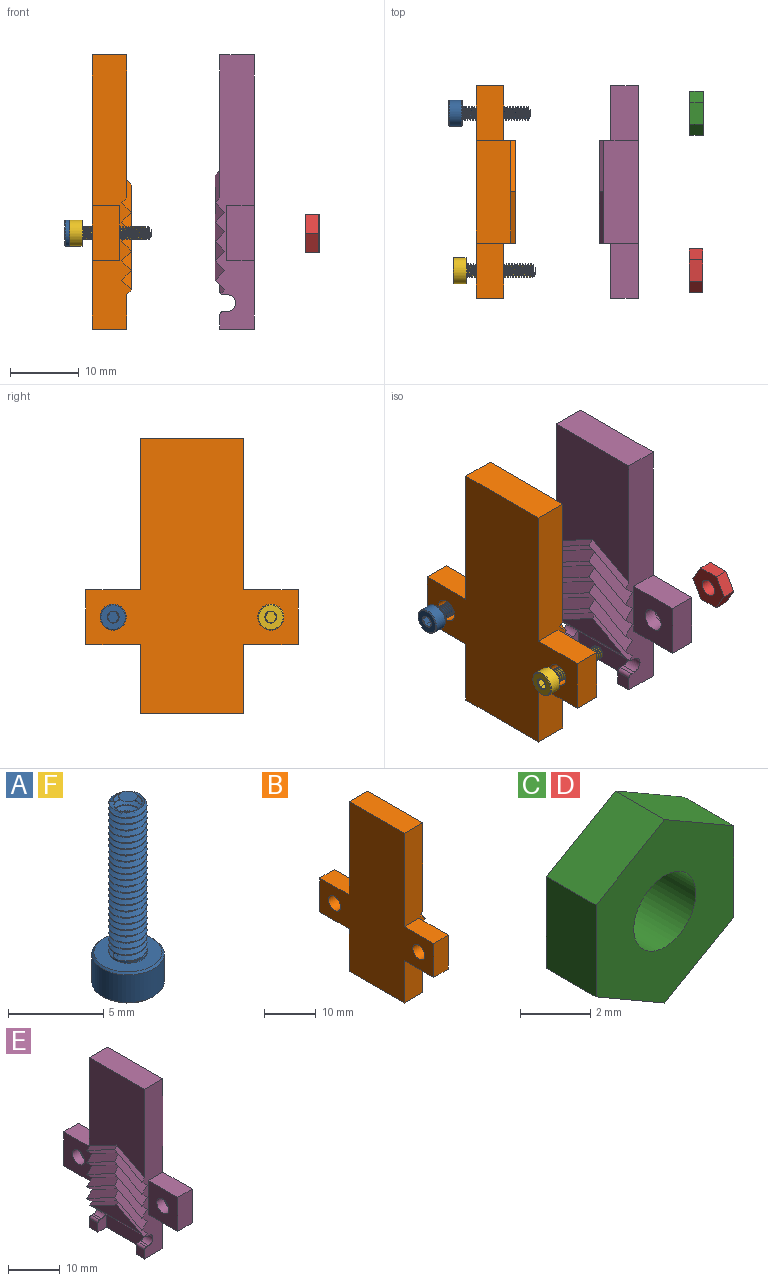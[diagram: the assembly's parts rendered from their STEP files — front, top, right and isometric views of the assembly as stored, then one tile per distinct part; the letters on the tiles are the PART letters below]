
ASSEMBLY  parts=6 mates=8
PART A: 49 faces, bbox 4.1x4.1x12.3 mm
  f0: cylinder r=1mm len=1.99mm, axis (0,0,1), area 0.1mm2, adj f1,f25,f26,f28
  f1: cylinder r=1mm len=2mm, axis (0,0,1), area 0.3mm2, adj f0,f2,f25,f26
  f2: cylinder r=1mm len=2mm, axis (0,0,1), area 0.3mm2, adj f1,f3,f25,f26
  f3: cylinder r=1mm len=2mm, axis (0,0,1), area 0.3mm2, adj f2,f4,f25,f26
  f4: cylinder r=1mm len=2mm, axis (0,0,1), area 0.3mm2, adj f3,f5,f25,f26
  f5: cylinder r=1mm len=2mm, axis (0,0,1), area 0.3mm2, adj f4,f6,f25,f26
  f6: cylinder r=1mm len=2mm, axis (0,0,1), area 0.3mm2, adj f5,f7,f25,f26
  f7: cylinder r=1mm len=2mm, axis (0,0,1), area 0.3mm2, adj f6,f8,f25,f26
  f8: cylinder r=1mm len=2mm, axis (0,0,1), area 0.3mm2, adj f7,f9,f25,f26
  f9: cylinder r=1mm len=2mm, axis (0,0,1), area 0.3mm2, adj f8,f10,f25,f26
  f10: cylinder r=1mm len=2mm, axis (0,0,1), area 0.3mm2, adj f9,f11,f25,f26
  f11: cylinder r=1mm len=2mm, axis (0,0,1), area 0.3mm2, adj f10,f12,f25,f26
  f12: cylinder r=1mm len=2mm, axis (0,0,1), area 0.3mm2, adj f11,f13,f25,f26
  f13: cylinder r=1mm len=2mm, axis (0,0,1), area 0.3mm2, adj f12,f14,f25,f26
  f14: cylinder r=1mm len=2mm, axis (0,0,1), area 0.3mm2, adj f13,f15,f25,f26
  f15: cylinder r=1mm len=2mm, axis (0,0,1), area 0.3mm2, adj f14,f16,f25,f26
  f16: cylinder r=1mm len=2mm, axis (0,0,1), area 0.3mm2, adj f15,f17,f25,f26
  f17: cylinder r=1mm len=2mm, axis (0,0,1), area 0.3mm2, adj f16,f18,f25,f26
  f18: cylinder r=1mm len=2mm, axis (0,0,1), area 0.3mm2, adj f17,f19,f25,f26
  f19: cylinder r=1mm len=2mm, axis (0,0,1), area 0.3mm2, adj f18,f20,f25,f26
  f20: cylinder r=1mm len=2mm, axis (0,0,1), area 0.3mm2, adj f19,f21,f25,f26
  f21: cylinder r=1mm len=2mm, axis (0,0,1), area 0.3mm2, adj f20,f22,f25,f26
  f22: cylinder r=1mm len=2mm, axis (0,0,1), area 0.3mm2, adj f21,f23,f25,f26
  f23: cylinder r=1mm len=2mm, axis (0,0,1), area 0.3mm2, adj f22,f24,f25,f26
  f24: cylinder r=1mm len=2mm, axis (0,0,1), area 0.8mm2, adj f23,f25,f26,f32,f48
  f25: bspline ~10.08x2.31mm, area 39.4mm2, adj f0,f1,f2,f3,f4,f5,f6,f7
  f26: bspline ~9.88x2.31mm, area 39.3mm2, adj f0,f1,f2,f3,f4,f5,f6,f7
  f27: cylinder r=0.74mm len=9.61mm, axis (0,0,-1), area -0.5mm2, adj f25,f26,f28,f48
  f28: cone r=0.49mm half-angle=55deg, axis (0,0,-1), area 2mm2, adj f0,f25,f26,f27,f29
  f29: plane 0.97x0.97mm, normal (0,0,1), area 0.7mm2, adj f28
  f30: cylinder r=1.9mm len=3.8mm, axis (0,0,1), area 21.2mm2, adj f46,f47
  f31: plane 3.57x3.57mm, normal (0,0,-1), area 7.7mm2, adj f33,f34,f35,f36,f37,f38,f46
  f32: plane 3.57x3.57mm, normal (0,0,1), area 6.9mm2, adj f24,f47
  f33: cone r=0.87mm half-angle=45deg, axis (0,0,-1), area 0mm2, adj f31,f40
  f34: cone r=0.87mm half-angle=45deg, axis (0,0,-1), area 0mm2, adj f31,f41
  f35: cone r=0.87mm half-angle=45deg, axis (0,0,-1), area 0mm2, adj f31,f42
  f36: cone r=0.87mm half-angle=45deg, axis (0,0,-1), area 0mm2, adj f31,f43
  f37: cone r=0.87mm half-angle=45deg, axis (0,0,-1), area 0mm2, adj f31,f44
  f38: cone r=0.87mm half-angle=45deg, axis (0,0,-1), area 0mm2, adj f31,f45
  f39: plane 1.73x1.5mm, normal (0,0,-1), area 1.9mm2, adj f40,f41,f42,f43,f44,f45
  f40: plane 1.45x1.08mm, normal (-0.5,-0.87,0), area 0.9mm2, adj f33,f39,f41,f45
  f41: plane 1.45x1.2mm, normal (-1,0,0), area 0.9mm2, adj f34,f39,f40,f42
  f42: plane 1.45x1.08mm, normal (-0.5,0.87,0), area 0.9mm2, adj f35,f39,f41,f43
  f43: plane 1.45x1.08mm, normal (0.5,0.87,0), area 0.9mm2, adj f36,f39,f42,f44
  f44: plane 1.45x1.2mm, normal (1,0,0), area 0.9mm2, adj f37,f39,f43,f45
  f45: plane 1.45x1.08mm, normal (0.5,-0.87,0), area 0.9mm2, adj f38,f39,f40,f44
  f46: cone r=1.79mm half-angle=45deg, axis (0,0,1), area 1.9mm2, adj f30,f31
  f47: cone r=1.9mm half-angle=45deg, axis (0,0,-1), area 1.9mm2, adj f30,f32
  f48: cone r=1mm half-angle=67.5deg, axis (0,0,-1), area 0.8mm2, adj f24,f25,f26,f27
PART B: 39 faces, bbox 5.7x31x40 mm
  f0: plane 40x5.71mm, normal (0,-1,0), area 168mm2, adj f1,f2,f3,f4,f5,f6,f7,f8
  f1: plane 40x31mm, normal (-1,0,0), area 710.9mm2, adj f0,f2,f16,f17,f19,f20,f21,f22
  f2: plane 15x5mm, normal (0,0,1), area 75mm2, adj f0,f1,f3,f22
  f3: plane 20.86x15mm, normal (1,0,0), area 282.9mm2, adj f0,f2,f4,f22,f23
  f4: plane 7.5x4.71mm, normal (0.66,0.35,-0.66), area 8mm2, adj f0,f3,f5,f23
  f5: plane 7.5x5.41mm, normal (0.66,-0.35,0.66), area 16mm2, adj f0,f4,f6,f24
  f6: plane 7.5x5.41mm, normal (0.66,0.35,-0.66), area 16mm2, adj f0,f5,f7,f25
  f7: plane 7.5x5.41mm, normal (0.66,-0.35,0.66), area 16mm2, adj f0,f6,f8,f26
  f8: plane 7.5x5.41mm, normal (0.66,0.35,-0.66), area 16mm2, adj f0,f7,f9,f27
  f9: plane 7.5x5.41mm, normal (0.66,-0.35,0.66), area 16mm2, adj f0,f8,f10,f28
  f10: plane 7.5x5.41mm, normal (0.66,0.35,-0.66), area 16mm2, adj f0,f9,f11,f29
  f11: plane 7.5x5.41mm, normal (0.66,-0.35,0.66), area 16mm2, adj f0,f10,f12,f30
  f12: plane 7.5x5.41mm, normal (0.66,0.35,-0.66), area 16mm2, adj f0,f11,f13,f31
  f13: plane 7.5x5.41mm, normal (0.66,-0.35,0.66), area 16mm2, adj f0,f12,f14,f32
  f14: plane 7.5x4.71mm, normal (0.66,0.35,-0.66), area 8mm2, adj f0,f13,f15,f33
  f15: plane 15x9mm, normal (1,0,0), area 105mm2, adj f0,f14,f16,f22,f33
  f16: plane 15x5mm, normal (0,0,-1), area 75mm2, adj f0,f1,f15,f22
  f17: plane 8x4mm, normal (0,0,-1), area 32mm2, adj f0,f1,f18,f20
  f18: plane 8x8mm, normal (1,0,0), area 55.4mm2, adj f0,f17,f19,f20,f21
  f19: plane 8x4mm, normal (0,0,1), area 32mm2, adj f0,f1,f18,f20
  f20: plane 8x4mm, normal (0,-1,0), area 32mm2, adj f1,f17,f18,f19
  f21: cylinder r=1.65mm len=4mm, axis (-1,0,0), area 41.5mm2, adj f1,f18
  f22: plane 40x5.71mm, normal (0,1,0), area 168mm2, adj f1,f2,f3,f15,f16,f23,f24,f25
  f23: plane 7.5x4.71mm, normal (0.66,-0.35,-0.66), area 8mm2, adj f3,f4,f22,f24
  f24: plane 7.5x5.41mm, normal (0.66,0.35,0.66), area 16mm2, adj f5,f22,f23,f25
  f25: plane 7.5x5.41mm, normal (0.66,-0.35,-0.66), area 16mm2, adj f6,f22,f24,f26
  f26: plane 7.5x5.41mm, normal (0.66,0.35,0.66), area 16mm2, adj f7,f22,f25,f27
  f27: plane 7.5x5.41mm, normal (0.66,-0.35,-0.66), area 16mm2, adj f8,f22,f26,f28
  f28: plane 7.5x5.41mm, normal (0.66,0.35,0.66), area 16mm2, adj f9,f22,f27,f29
  f29: plane 7.5x5.41mm, normal (0.66,-0.35,-0.66), area 16mm2, adj f10,f22,f28,f30
  f30: plane 7.5x5.41mm, normal (0.66,0.35,0.66), area 16mm2, adj f11,f22,f29,f31
  f31: plane 7.5x5.41mm, normal (0.66,-0.35,-0.66), area 16mm2, adj f12,f22,f30,f32
  f32: plane 7.5x5.41mm, normal (0.66,0.35,0.66), area 16mm2, adj f13,f22,f31,f33
  f33: plane 7.5x4.71mm, normal (0.66,-0.35,-0.66), area 8mm2, adj f14,f15,f22,f32
  f34: plane 8x4mm, normal (0,0,-1), area 32mm2, adj f1,f22,f35,f37
  f35: plane 8x8mm, normal (1,0,0), area 55.4mm2, adj f22,f34,f36,f37,f38
  f36: plane 8x4mm, normal (0,0,1), area 32mm2, adj f1,f22,f35,f37
  f37: plane 8x4mm, normal (0,1,0), area 32mm2, adj f1,f34,f35,f36
  f38: cylinder r=1.65mm len=4mm, axis (-1,0,0), area 41.5mm2, adj f1,f35
PART C: 9 faces, bbox 5.6x2x6.4 mm
  f0: plane 2.78x2mm, normal (0.5,0,-0.87), area 6.4mm2, adj f1,f6,f7,f8
  f1: plane 3.2x2mm, normal (1,0,0), area 6.4mm2, adj f0,f2,f7,f8
  f2: plane 2.78x2mm, normal (0.5,0,0.87), area 6.4mm2, adj f1,f3,f7,f8
  f3: plane 2.78x2mm, normal (-0.5,0,0.87), area 6.4mm2, adj f2,f4,f7,f8
  f4: plane 3.2x2mm, normal (-1,0,0), area 6.4mm2, adj f3,f6,f7,f8
  f5: cylinder r=1.25mm len=2.5mm, axis (0,1,0), area 15.7mm2, adj f7,f8
  f6: plane 2.78x2mm, normal (-0.5,0,-0.87), area 6.4mm2, adj f0,f4,f7,f8
  f7: plane 6.41x5.55mm, normal (0,-1,0), area 21.8mm2, adj f0,f1,f2,f3,f4,f5,f6
  f8: plane 6.41x5.55mm, normal (0,1,0), area 21.8mm2, adj f0,f1,f2,f3,f4,f5,f6
PART D: same geometry as C
PART E: 65 faces, bbox 5.7x31x40 mm
  f0: plane 2.3x2.1mm, normal (-1,0,0), area 4.8mm2, adj f1,f4,f6,f62
  f1: plane 15x5mm, normal (0,0,-1), area 51.1mm2, adj f0,f6,f7,f8,f9,f62,f63,f64
  f2: plane 2.3x0.6mm, normal (0,0,1), area 1.4mm2, adj f3,f4,f6,f62
  f3: cylinder r=1.2mm len=15mm, axis (0,-1,0), area 36.9mm2, adj f2,f6,f7,f58,f59,f62,f63,f64
  f4: cylinder r=0.5mm len=2.3mm, axis (0,-1,0), area 1.8mm2, adj f0,f2,f6,f62
  f5: plane 13.13x3.5mm, normal (-1,0,0), area 23mm2, adj f10,f35,f61
  f6: plane 40x5.71mm, normal (0,-1,0), area 163mm2, adj f0,f1,f2,f3,f4,f8,f10,f11
  f7: plane 40x5.71mm, normal (0,1,0), area 163mm2, adj f1,f3,f8,f9,f21,f22,f35,f36
  f8: plane 40x31mm, normal (1,0,0), area 674.6mm2, adj f1,f6,f7,f22,f23,f24,f26,f27
  f9: plane 2.3x2.1mm, normal (-1,0,0), area 4.8mm2, adj f1,f7,f60,f63
  f10: plane 7.5x4.56mm, normal (-0.66,-0.35,0.66), area 7.9mm2, adj f5,f6,f11,f35,f61
  f11: plane 7.5x5.41mm, normal (-0.66,0.35,-0.66), area 16mm2, adj f6,f10,f12,f36
  f12: plane 7.5x5.41mm, normal (-0.66,-0.35,0.66), area 16mm2, adj f6,f11,f13,f37
  f13: plane 7.5x5.41mm, normal (-0.66,0.35,-0.66), area 16mm2, adj f6,f12,f14,f38
  f14: plane 7.5x5.41mm, normal (-0.66,-0.35,0.66), area 16mm2, adj f6,f13,f15,f39
  f15: plane 7.5x5.41mm, normal (-0.66,0.35,-0.66), area 16mm2, adj f6,f14,f16,f40
  f16: plane 7.5x5.41mm, normal (-0.66,-0.35,0.66), area 16mm2, adj f6,f15,f17,f41
  f17: plane 7.5x5.41mm, normal (-0.66,0.35,-0.66), area 16mm2, adj f6,f16,f18,f42
  f18: plane 7.5x5.41mm, normal (-0.66,-0.35,0.66), area 16mm2, adj f6,f17,f19,f43
  f19: plane 7.5x5.41mm, normal (-0.66,0.35,-0.66), area 16mm2, adj f6,f18,f20,f44
  f20: plane 7.5x4.71mm, normal (-0.66,-0.35,0.66), area 8mm2, adj f6,f19,f21,f45
  f21: plane 20.86x15mm, normal (-1,0,0), area 282.9mm2, adj f6,f7,f20,f22,f45
  f22: plane 15x5mm, normal (0,0,1), area 75mm2, adj f6,f7,f8,f21
  f23: plane 8x4mm, normal (0,0,-1), area 32mm2, adj f6,f8,f25,f26
  f24: plane 8x4mm, normal (0,0,1), area 32mm2, adj f6,f8,f25,f26
  f25: plane 8x8mm, normal (-1,0,0), area 55.4mm2, adj f6,f23,f24,f26,f34
  f26: plane 8x4mm, normal (0,-1,0), area 32mm2, adj f8,f23,f24,f25
  f27: plane 2.78x2mm, normal (0,-0.87,-0.5), area 6.4mm2, adj f8,f28,f32,f33
  f28: plane 3.2x2mm, normal (0,0,-1), area 6.4mm2, adj f8,f27,f29,f33
  f29: plane 2.77x2mm, normal (0,0.87,-0.5), area 6.4mm2, adj f8,f28,f30,f33
  f30: plane 2.78x2mm, normal (0,0.87,0.5), area 6.4mm2, adj f8,f29,f31,f33
  f31: plane 3.2x2mm, normal (0,0,1), area 6.4mm2, adj f8,f30,f32,f33
  f32: plane 2.77x2mm, normal (0,-0.87,0.5), area 6.4mm2, adj f8,f27,f31,f33
  f33: plane 6.41x5.56mm, normal (1,0,0), area 18.1mm2, adj f27,f28,f29,f30,f31,f32,f34
  f34: cylinder r=1.65mm len=3.3mm, axis (1,0,0), area 20.7mm2, adj f25,f33
  f35: plane 7.5x4.56mm, normal (-0.66,0.35,0.66), area 7.9mm2, adj f5,f7,f10,f36,f61
  f36: plane 7.5x5.41mm, normal (-0.66,-0.35,-0.66), area 16mm2, adj f7,f11,f35,f37
  f37: plane 7.5x5.41mm, normal (-0.66,0.35,0.66), area 16mm2, adj f7,f12,f36,f38
  f38: plane 7.5x5.41mm, normal (-0.66,-0.35,-0.66), area 16mm2, adj f7,f13,f37,f39
  f39: plane 7.5x5.41mm, normal (-0.66,0.35,0.66), area 16mm2, adj f7,f14,f38,f40
  f40: plane 7.5x5.41mm, normal (-0.66,-0.35,-0.66), area 16mm2, adj f7,f15,f39,f41
  f41: plane 7.5x5.41mm, normal (-0.66,0.35,0.66), area 16mm2, adj f7,f16,f40,f42
  f42: plane 7.5x5.41mm, normal (-0.66,-0.35,-0.66), area 16mm2, adj f7,f17,f41,f43
  f43: plane 7.5x5.41mm, normal (-0.66,0.35,0.66), area 16mm2, adj f7,f18,f42,f44
  f44: plane 7.5x5.41mm, normal (-0.66,-0.35,-0.66), area 16mm2, adj f7,f19,f43,f45
  f45: plane 7.5x4.71mm, normal (-0.66,0.35,0.66), area 8mm2, adj f7,f20,f21,f44
  f46: plane 8x4mm, normal (0,0,-1), area 32mm2, adj f7,f8,f48,f49
  f47: plane 8x4mm, normal (0,0,1), area 32mm2, adj f7,f8,f48,f49
  f48: plane 8x8mm, normal (-1,0,0), area 55.4mm2, adj f7,f46,f47,f49,f57
  f49: plane 8x4mm, normal (0,1,0), area 32mm2, adj f8,f46,f47,f48
  f50: plane 2.78x2mm, normal (0,0.87,-0.5), area 6.4mm2, adj f8,f51,f55,f56
  f51: plane 3.2x2mm, normal (0,0,-1), area 6.4mm2, adj f8,f50,f52,f56
  f52: plane 2.77x2mm, normal (0,-0.87,-0.5), area 6.4mm2, adj f8,f51,f53,f56
  f53: plane 2.78x2mm, normal (0,-0.87,0.5), area 6.4mm2, adj f8,f52,f54,f56
  f54: plane 3.2x2mm, normal (0,0,1), area 6.4mm2, adj f8,f53,f55,f56
  f55: plane 2.77x2mm, normal (0,0.87,0.5), area 6.4mm2, adj f8,f50,f54,f56
  f56: plane 6.41x5.56mm, normal (1,0,0), area 18.1mm2, adj f50,f51,f52,f53,f54,f55,f57
  f57: cylinder r=1.65mm len=3.3mm, axis (1,0,0), area 20.7mm2, adj f48,f56
  f58: plane 15x0.6mm, normal (0,0,-1), area 9mm2, adj f3,f6,f7,f61
  f59: plane 2.3x0.6mm, normal (0,0,1), area 1.4mm2, adj f3,f7,f60,f63
  f60: cylinder r=0.5mm len=2.3mm, axis (0,-1,0), area 1.8mm2, adj f7,f9,f59,f63
  f61: cylinder r=0.5mm len=15mm, axis (0,-1,0), area 11.4mm2, adj f5,f6,f7,f10,f35,f58
  f62: plane 3.8x2.3mm, normal (0,1,0), area 6.2mm2, adj f0,f1,f2,f3,f4,f64
  f63: plane 3.8x2.3mm, normal (0,-1,0), area 6.2mm2, adj f1,f3,f9,f59,f60,f64
  f64: plane 10.4x3.8mm, normal (-1,0,0), area 39.5mm2, adj f1,f3,f62,f63
PART F: same geometry as A
PLACE A rot(axis=(0.71,0,0.71),180deg) t=(16.1,26.59,-10.33)mm
PLACE B t=(8.14,7.59,-24.33)mm
PLACE C rot(axis=(-0.58,0.58,0.58),120deg) t=(39.28,26.59,-10.33)mm
PLACE D rot(axis=(-0.58,-0.58,-0.58),120deg) t=(41.19,3.59,-10.33)mm
PLACE E t=(21.76,7.59,-24.33)mm
PLACE F rot(axis=(-0.71,0,-0.71),180deg) t=(16.76,3.59,-10.33)mm
MATE cylindrical F.f0 <-> B.f21  axis (1,0,0) through (5.76,3.59,-10.33)mm
MATE parallel B.f2 <-> E.f22  axis (0,0,1) through (10.64,15.09,15.67)mm
MATE cylindrical A.f0 <-> B.f38  axis (1,0,0) through (5.1,26.59,-10.33)mm
MATE slider E.f34 <-> B.f21  axis (1,0,0) through (29.76,3.59,-10.33)mm
MATE parallel B.f16 <-> E.f1  axis (0,0,-1) through (10.64,15.09,-24.33)mm
MATE parallel B.f0 <-> E.f6  axis (0,-1,0) through (13.14,7.59,5.24)mm
MATE cylindrical C.f5 <-> E.f57  axis (-1,0,0) through (39.28,26.59,-10.33)mm
MATE cylindrical D.f5 <-> E.f34  axis (-1,0,0) through (39.19,3.59,-10.33)mm
